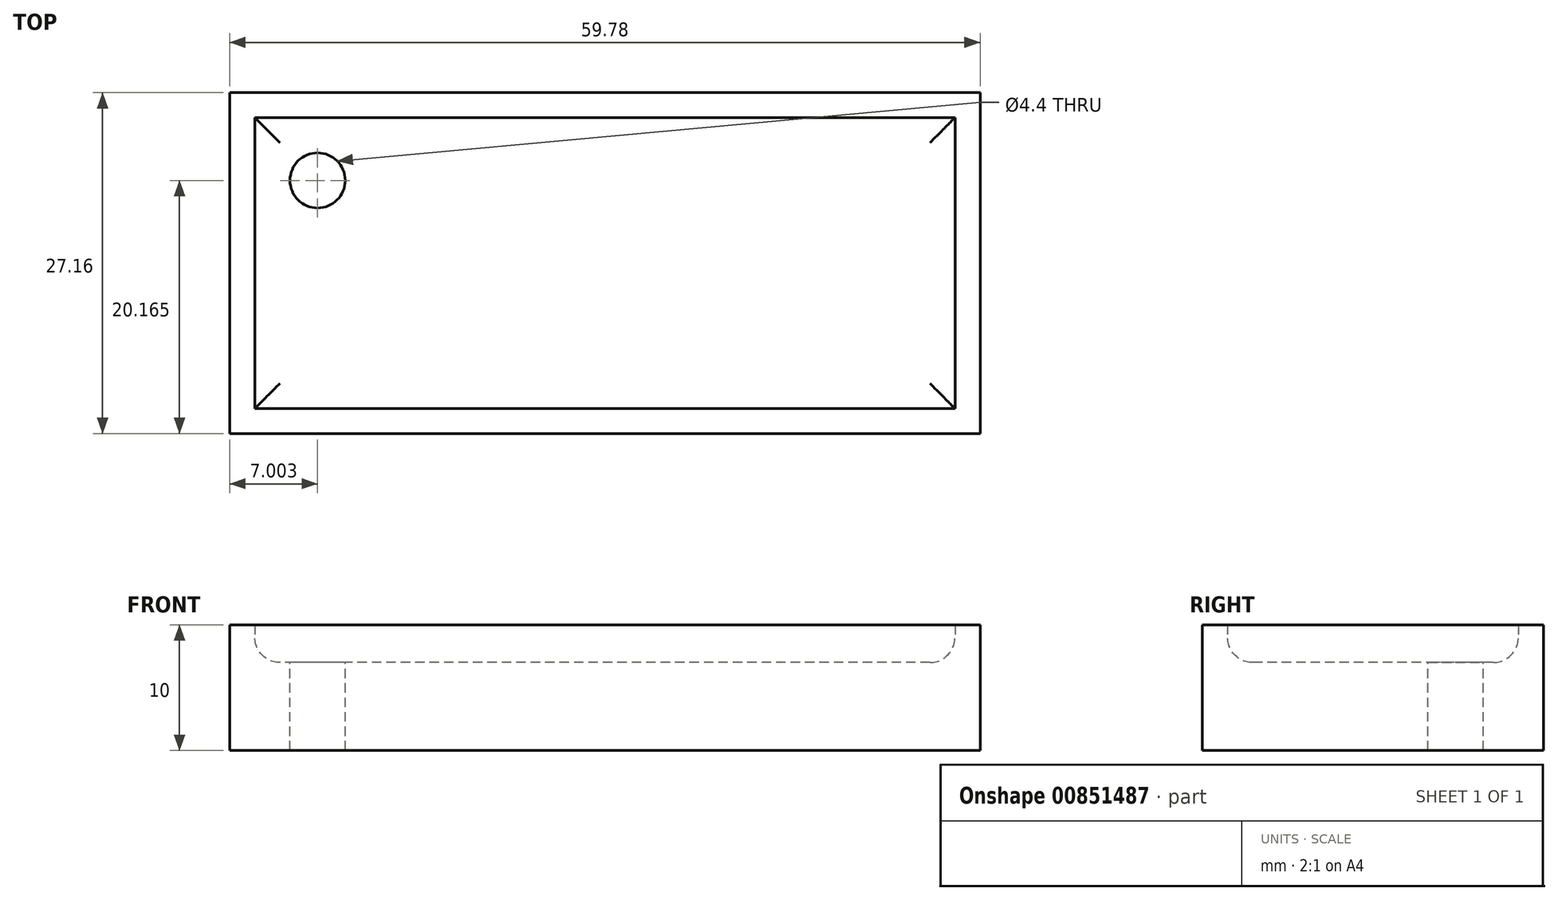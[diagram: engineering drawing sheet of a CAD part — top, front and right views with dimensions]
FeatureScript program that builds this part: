
annotation { "Feature Type Name" : "Feature", "Feature Type Description" : "" }
export const myFeature = defineFeature(function(context is Context, id is Id, definition is map)
    precondition{}
    {
        {
            var Q0;
            Q0=qCreatedBy(makeId("Top.planeOp"),FACE);
            var sketch = newSketch(context, id + "F0", { "sketchPlane" : qUnion([Q0])});
            skLineSegment(sketch, "E0.bottom", {"start": v(29.89, 13.58) * mm, "end": v(-29.89, 13.58) * mm});
            skLineSegment(sketch, "E0.top", {"start": v(29.89, -13.58) * mm, "end": v(-29.89, -13.58) * mm});
            skLineSegment(sketch, "E0.left", {"start": v(29.89, 13.58) * mm, "end": v(29.89, -13.58) * mm});
            skLineSegment(sketch, "E0.right", {"start": v(-29.89, 13.58) * mm, "end": v(-29.89, -13.58) * mm});
            skPoint(sketch, "E0.middle", {"position": v(0, 0) * mm});
            skSolve(sketch);
        }
        {
            var Q0;
            Q0=makeQuery(id+"F0.imprint","IMPRINT",FACE,{"disambiguationData":[TD([[makeQuery(id+"F0.imprint","IMPRINT",EDGE,{"derivedFrom":sQuery(id+"F0.wireOp",EDGE,"E0.bottom")}),1.0]])]});
            extrude(context, id + "F1", {"entities" : qUnion([Q0]), "endBound" : BoundingType.SYMMETRIC, "depth" : 5 * mm, "offsetDistance" : 25 * mm});
        }
        {
            var Q0;
            Q0=makeQuery(id+"F1.opExtrude","CAP_FACE",FACE,{"disambiguationData":[OSD([sQuery(id+"F0.wireOp",EDGE,"E0.bottom"),sQuery(id+"F0.wireOp",EDGE,"E0.top"),sQuery(id+"F0.wireOp",EDGE,"E0.left"),sQuery(id+"F0.wireOp",EDGE,"E0.right")])],"isStart":false});
            var Q1;
            Q1=makeQuery(id+"F1.opExtrude","SWEPT_BODY",BODY,{"disambiguationData":[OSD([sQuery(id+"F0.wireOp",EDGE,"E0.bottom"),sQuery(id+"F0.wireOp",EDGE,"E0.top"),sQuery(id+"F0.wireOp",EDGE,"E0.left"),sQuery(id+"F0.wireOp",EDGE,"E0.right")])]});
            shell(context, id + "F2", {"entities" : qUnion([Q0]), "parts" : qUnion([Q1]), "thickness" : 2 * mm});
        }
        {
            var Q0;
            Q0=makeQuery(id+"F1.opExtrude","CAP_FACE",FACE,{"disambiguationData":[OSD([sQuery(id+"F0.wireOp",EDGE,"E0.bottom"),sQuery(id+"F0.wireOp",EDGE,"E0.top"),sQuery(id+"F0.wireOp",EDGE,"E0.left"),sQuery(id+"F0.wireOp",EDGE,"E0.right")])],"isStart":true});
            extrude(context, id + "F3", {"entities" : qUnion([Q0]), "operationType" : NewBodyOperationType.ADD, "depth" : 5 * mm, "offsetDistance" : 25 * mm});
        }
        {
            var Q0;
            {var subQ0=sQuery(id+"F0.wireOp",EDGE,"E0.bottom");Q0=makeQuery(id+"F2.opShell","OFFSET_EDGE",EDGE,{"disambiguationData":[OSD([subQ0]),TDD([makeQuery(id+"F1.opExtrude","CAP_EDGE",EDGE,{"disambiguationData":[OSD([subQ0])],"isStart":true})])]});}
            var Q1;
            {var subQ0=sQuery(id+"F0.wireOp",EDGE,"E0.top");Q1=makeQuery(id+"F2.opShell","OFFSET_EDGE",EDGE,{"disambiguationData":[OSD([subQ0]),TDD([makeQuery(id+"F1.opExtrude","CAP_EDGE",EDGE,{"disambiguationData":[OSD([subQ0])],"isStart":true})])]});}
            var Q2;
            {var subQ0=sQuery(id+"F0.wireOp",EDGE,"E0.left");Q2=makeQuery(id+"F2.opShell","OFFSET_EDGE",EDGE,{"disambiguationData":[OSD([subQ0]),TDD([makeQuery(id+"F1.opExtrude","CAP_EDGE",EDGE,{"disambiguationData":[OSD([subQ0])],"isStart":true})])]});}
            var Q3;
            Q3=makeQuery(id+"F2.opShell","OFFSET_FACE",FACE,{"disambiguationData":[OSD([sQuery(id+"F0.wireOp",EDGE,"E0.bottom"),sQuery(id+"F0.wireOp",EDGE,"E0.top"),sQuery(id+"F0.wireOp",EDGE,"E0.left"),sQuery(id+"F0.wireOp",EDGE,"E0.right")])]});
            fillet(context, id + "F4", {"entities" : qUnion([Q0, Q1, Q2, Q3]), "radius" : 2 * mm, "tangentPropagation" : true, "allowEdgeOverflow" : false});
        }
        {
            var Q0;
            Q0=makeQuery(id+"F0.imprint","IMPRINT",FACE,{"disambiguationData":[TD([[makeQuery(id+"F0.imprint","IMPRINT",EDGE,{"derivedFrom":sQuery(id+"F0.wireOp",EDGE,"E0.bottom")}),1.0]])]});
            var sketch = newSketch(context, id + "F5", { "sketchPlane" : qUnion([Q0])});
            skPoint(sketch, "E1", {"position": v(-22.89, 6.58) * mm});
            skSolve(sketch);
        }
        {
            var Q0;
            Q0=sQuery(id+"F5.wireOp",VERTEX,"E1");
            var Q1;
            Q1=makeQuery(id+"F1.opExtrude","SWEPT_BODY",BODY,{"disambiguationData":[OSD([sQuery(id+"F0.wireOp",EDGE,"E0.bottom"),sQuery(id+"F0.wireOp",EDGE,"E0.top"),sQuery(id+"F0.wireOp",EDGE,"E0.left"),sQuery(id+"F0.wireOp",EDGE,"E0.right")])]});
            hole(context, id + "F6", {"style" : HoleStyle.SIMPLE, "endStyle" : HoleEndStyle.THROUGH, "standardTappedOrClearance" : lookupTablePath({ "fit" : "Normal", "standard" : "ISO", "size" : "M4", "type" : "Clearance" }), "standardBlindInLast" : lookupTablePath({ "fit" : "Standard", "standard" : "ISO", "size" : "M4", "type" : "Clearance" }), "holeDiameter" : 4.4 * mm, "majorDiameter" : 4 * mm, "isTappedThrough" : true, "tappedDepth" : 12 * mm, "tapClearance" : 3, "startFromSketch" : true, "locations" : qUnion([Q0]), "scope" : qUnion([Q1])});
        }
    });
